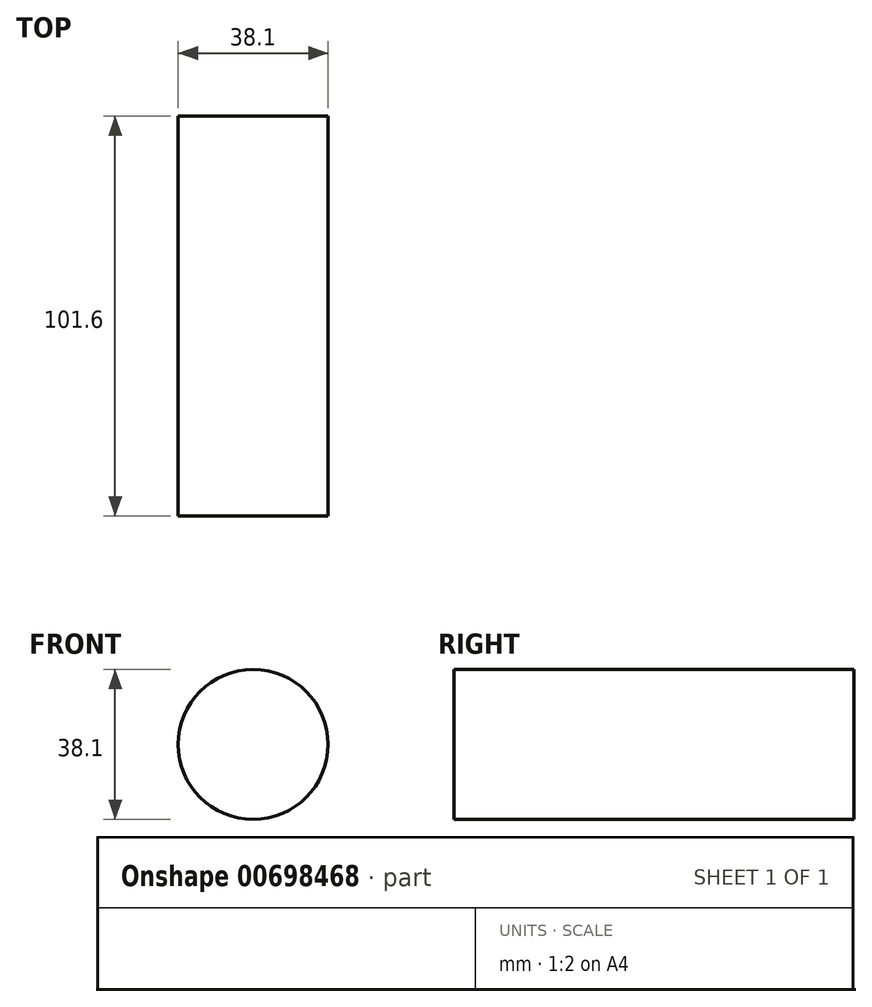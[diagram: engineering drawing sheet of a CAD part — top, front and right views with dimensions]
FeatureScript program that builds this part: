
annotation { "Feature Type Name" : "Feature", "Feature Type Description" : "" }
export const myFeature = defineFeature(function(context is Context, id is Id, definition is map)
    precondition{}
    {
        {
            var Q0;
            Q0=qCreatedBy(makeId("Front.planeOp"),FACE);
            var sketch = newSketch(context, id + "F0", { "sketchPlane" : qUnion([Q0])});
            skCircle(sketch, "E0", {"center": v(0, 0) * mm, "radius": 19.05 * mm});
            skSolve(sketch);
        }
        {
            var Q0;
            Q0=makeQuery(id+"F0.imprint","IMPRINT",FACE,{"disambiguationData":[TD([[makeQuery(id+"F0.imprint","IMPRINT",EDGE,{"derivedFrom":sQuery(id+"F0.wireOp",EDGE,"E0")}),1.0]])]});
            extrude(context, id + "F1", {"entities" : qUnion([Q0]), "depth" : 101.6 * mm, "offsetDistance" : 25.4 * mm});
        }
    });
